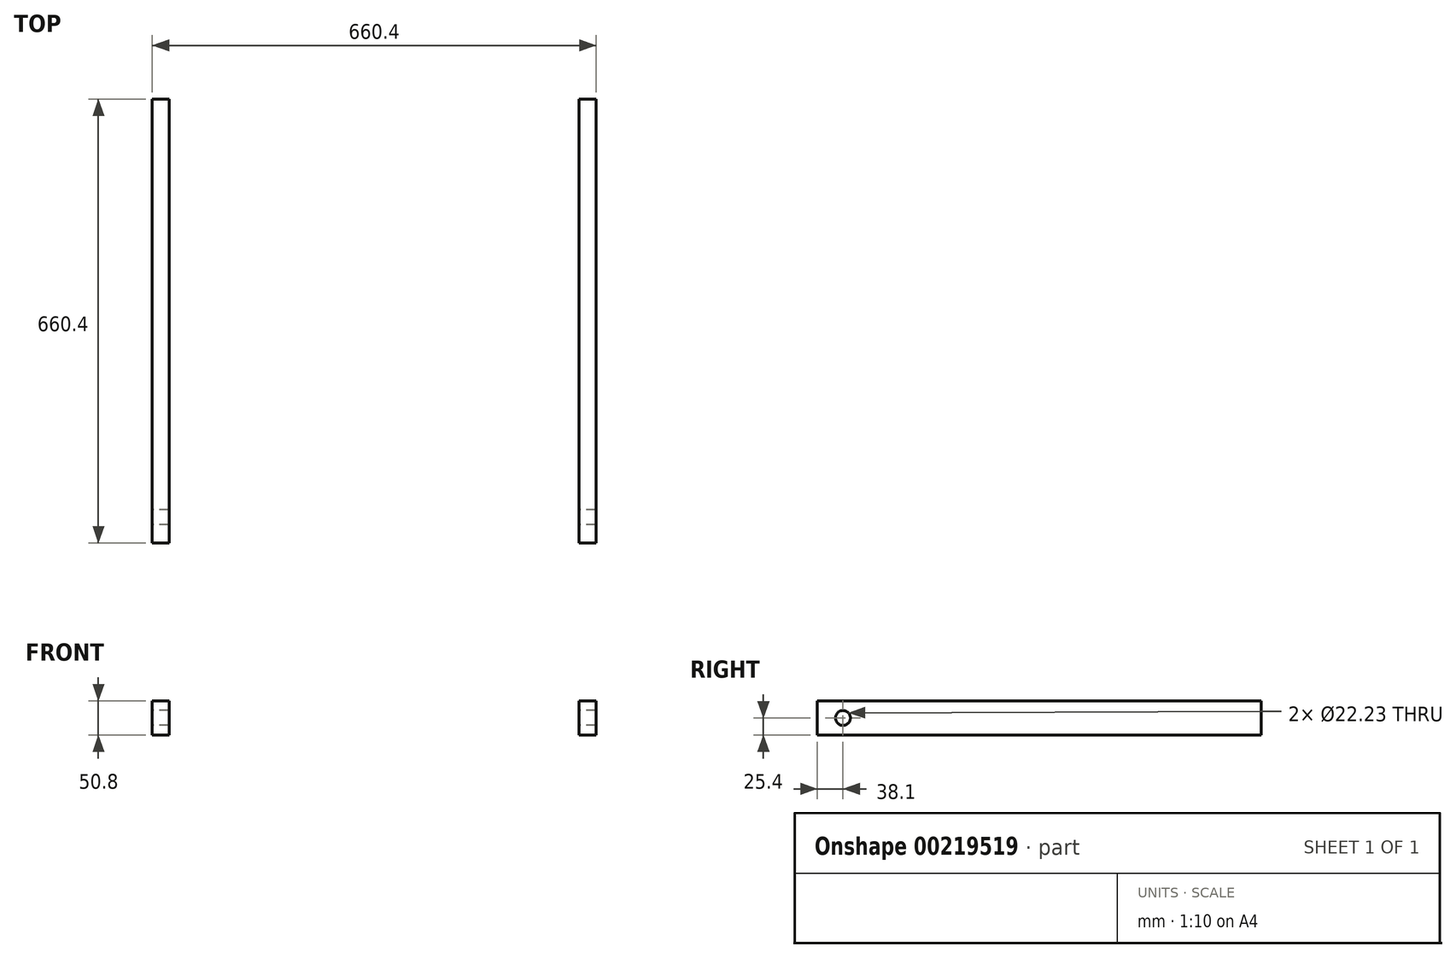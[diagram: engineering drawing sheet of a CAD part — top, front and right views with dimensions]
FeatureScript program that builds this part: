
annotation { "Feature Type Name" : "Feature", "Feature Type Description" : "" }
export const myFeature = defineFeature(function(context is Context, id is Id, definition is map)
    precondition{}
    {
        {
            var Q0;
            Q0=qCreatedBy(makeId("Top.planeOp"),FACE);
            var sketch = newSketch(context, id + "F0", { "sketchPlane" : qUnion([Q0])});
            skLineSegment(sketch, "E0", {"start": v(0, 0) * mm, "end": v(0, 677.24) * mm, "construction": true});
            skLineSegment(sketch, "E1", {"start": v(-304.8, 0) * mm, "end": v(-304.8, 660.4) * mm});
            skLineSegment(sketch, "E2", {"start": v(-304.8, 660.4) * mm, "end": v(-330.2, 660.4) * mm});
            skLineSegment(sketch, "E3", {"start": v(-330.2, 660.4) * mm, "end": v(-330.2, 0) * mm});
            skLineSegment(sketch, "E4", {"start": v(-330.2, 0) * mm, "end": v(-304.8, 0) * mm});
            skLineSegment(sketch, "E5.MirrorCS", {"start": v(304.8, 0) * mm, "end": v(304.8, 660.4) * mm});
            skLineSegment(sketch, "E6.MirrorCS", {"start": v(304.8, 660.4) * mm, "end": v(330.2, 660.4) * mm});
            skLineSegment(sketch, "E7.MirrorCS", {"start": v(330.2, 660.4) * mm, "end": v(330.2, 0) * mm});
            skLineSegment(sketch, "E8.MirrorCS", {"start": v(330.2, 0) * mm, "end": v(304.8, 0) * mm});
            skSolve(sketch);
        }
        {
            var Q0;
            Q0=makeQuery(id+"F0.imprint","IMPRINT",FACE,{"disambiguationData":[TD([[makeQuery(id+"F0.imprint","IMPRINT",EDGE,{"derivedFrom":sQuery(id+"F0.wireOp",EDGE,"E1")}),1.0]])]});
            var Q1;
            Q1=makeQuery(id+"F0.imprint","IMPRINT",FACE,{"disambiguationData":[TD([[makeQuery(id+"F0.imprint","IMPRINT",EDGE,{"derivedFrom":sQuery(id+"F0.wireOp",EDGE,"E5.MirrorCS")}),-1.0]])]});
            extrude(context, id + "F1", {"entities" : qUnion([Q0, Q1]), "depth" : 50.8 * mm});
        }
        {
            var Q0;
            Q0=makeQuery(id+"F1.opExtrude","SWEPT_FACE",FACE,{"disambiguationData":[OSD([sQuery(id+"F0.wireOp",EDGE,"E3")])]});
            var sketch = newSketch(context, id + "F2", { "sketchPlane" : qUnion([Q0])});
            skLineSegment(sketch, "E9", {"start": v(-38.1, 50.8) * mm, "end": v(-38.1, 0) * mm, "construction": true});
            skCircle(sketch, "E10", {"center": v(-38.1, 25.4) * mm, "radius": 11.11 * mm});
            skSolve(sketch);
        }
        {
            var Q0;
            Q0 = qSketchRegion(id + "F2", true);
            extrude(context, id + "F3", {"entities" : qUnion([Q0]), "operationType" : NewBodyOperationType.REMOVE, "endBound" : BoundingType.THROUGH_ALL, "oppositeDirection" : true, "depth" : 25.4 * mm});
        }
        {
            var Q0;
            Q0=makeQuery(id+"F1.opExtrude","SWEPT_FACE",FACE,{"disambiguationData":[OSD([sQuery(id+"F0.wireOp",EDGE,"E5.MirrorCS")])]});
            var sketch = newSketch(context, id + "F4", { "sketchPlane" : qUnion([Q0])});
            skLineSegment(sketch, "E11", {"start": v(-38.1, 50.8) * mm, "end": v(-38.1, 0) * mm, "construction": true});
            skCircle(sketch, "E12", {"center": v(-38.1, 25.4) * mm, "radius": 11.11 * mm});
            skSolve(sketch);
        }
        {
            var Q0;
            Q0=makeQuery(id+"F4.imprint","IMPRINT",FACE,{"disambiguationData":[TD([[makeQuery(id+"F4.imprint","IMPRINT",EDGE,{"derivedFrom":sQuery(id+"F4.wireOp",EDGE,"E12")}),1.0]])]});
            extrude(context, id + "F5", {"entities" : qUnion([Q0]), "operationType" : NewBodyOperationType.REMOVE, "endBound" : BoundingType.THROUGH_ALL, "oppositeDirection" : true, "depth" : 25.4 * mm});
        }
    });
